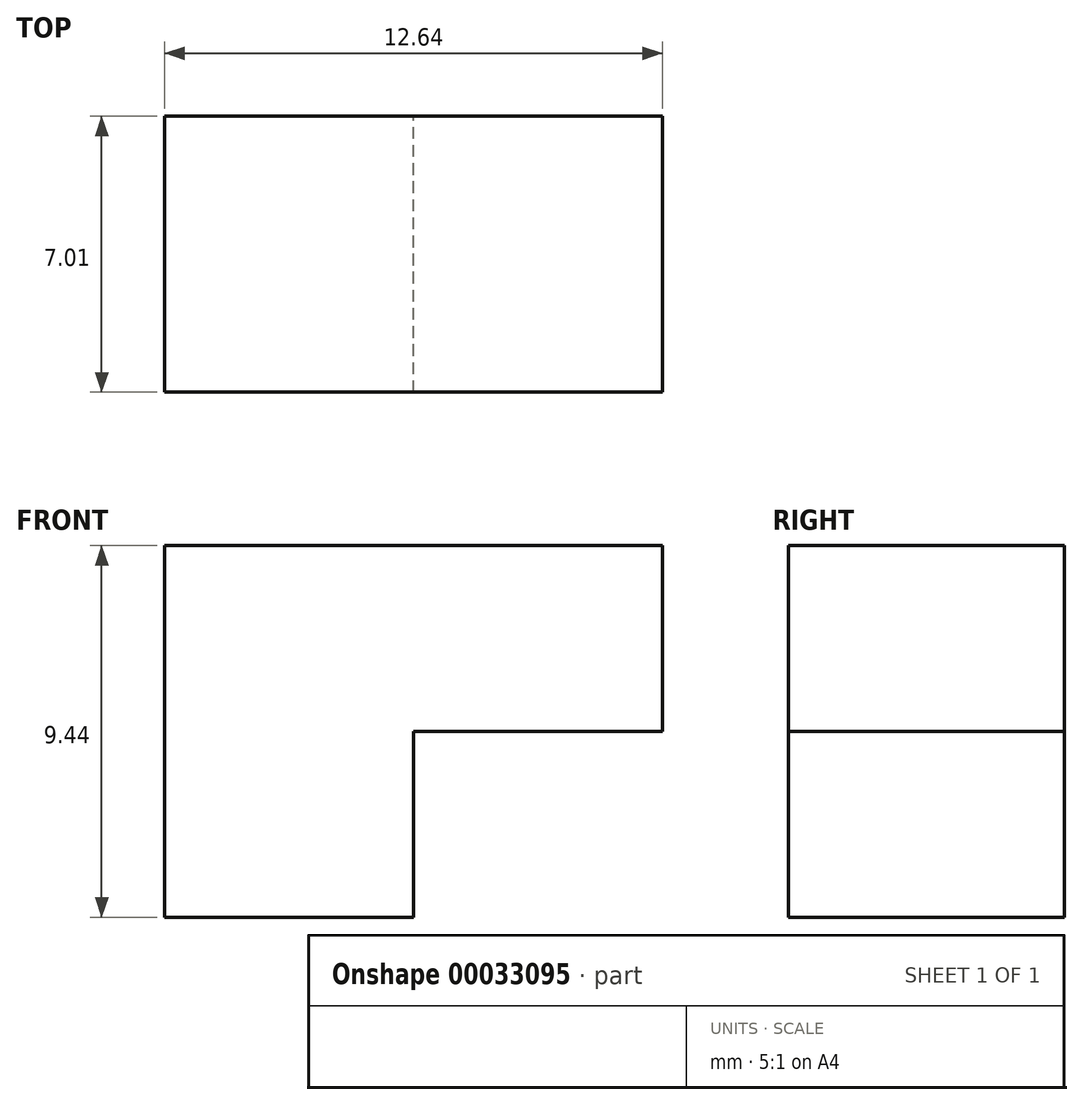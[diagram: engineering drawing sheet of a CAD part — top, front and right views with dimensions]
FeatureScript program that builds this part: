
annotation { "Feature Type Name" : "Feature", "Feature Type Description" : "" }
export const myFeature = defineFeature(function(context is Context, id is Id, definition is map)
    precondition{}
    {
        {
            var Q0;
            Q0=qCreatedBy(makeId("Front.planeOp"),FACE);
            var sketch = newSketch(context, id + "F0", { "sketchPlane" : qUnion([Q0])});
            skLineSegment(sketch, "E0.rect.bottom", {"start": v(0, -4.72) * mm, "end": v(-6.32, -4.72) * mm});
            skLineSegment(sketch, "E0.rect.top", {"start": v(6.32, 4.72) * mm, "end": v(-6.32, 4.72) * mm});
            skLineSegment(sketch, "E0.rect.left", {"start": v(6.32, 0) * mm, "end": v(6.32, 4.72) * mm});
            skLineSegment(sketch, "E0.rect.right", {"start": v(-6.32, -4.72) * mm, "end": v(-6.32, 4.72) * mm});
            skPoint(sketch, "E0.rect.middle", {"position": v(0, 0) * mm});
            skLineSegment(sketch, "E1.top", {"start": v(6.32, 0) * mm, "end": v(0, 0) * mm});
            skLineSegment(sketch, "E1.right", {"start": v(0, -4.72) * mm, "end": v(0, 0) * mm});
            skPoint(sketch, "E2.orphan", {"position": v(6.32, -4.72) * mm});
            skSolve(sketch);
        }
        {
            var Q0;
            Q0 = qSketchRegion(id + "F0", true);
            extrude(context, id + "F1", {"entities" : qUnion([Q0]), "depth" : 7 * mm});
        }
    });
